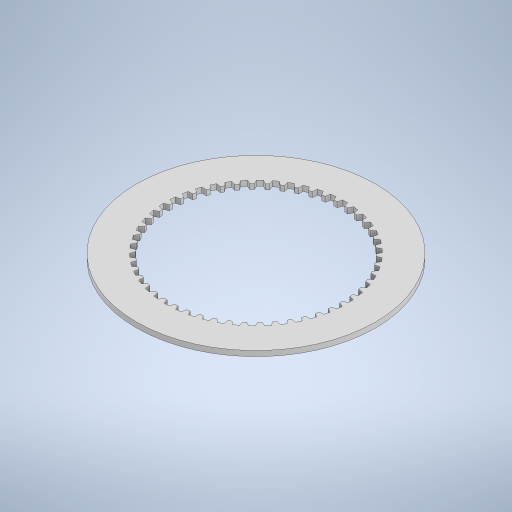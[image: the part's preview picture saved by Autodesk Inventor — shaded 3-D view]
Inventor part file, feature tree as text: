
AUTODESK INVENTOR PART (.ipt)
format: ipt  version: 2023 (Build 270158000, 158)  size: 502,272 bytes
history: native  units: in
note: dims shown in document units (in); Inventor stores cm internally (conversion verified against a paired STEP export)
features: extrude x1, sketch x1
ambient origin geometry x8: Origin, YZ Plane, XZ Plane, XY Plane, X Axis, Y Axis, Z Axis, Center Point
bodies: Solid1 (feature_tree)
feature tree (2):
  extrude  "Extrusion1"  Depth=0.1969in
  sketch  "Sketch1"  dims[d0=8.9567in d1=6.6929in d2=0.1181in d3=3.189in d4=0.2362in d5=0.7614in d6=0.7614in d7=19.685in d9=360.0deg d11=0.1969in d12=0.0in]
